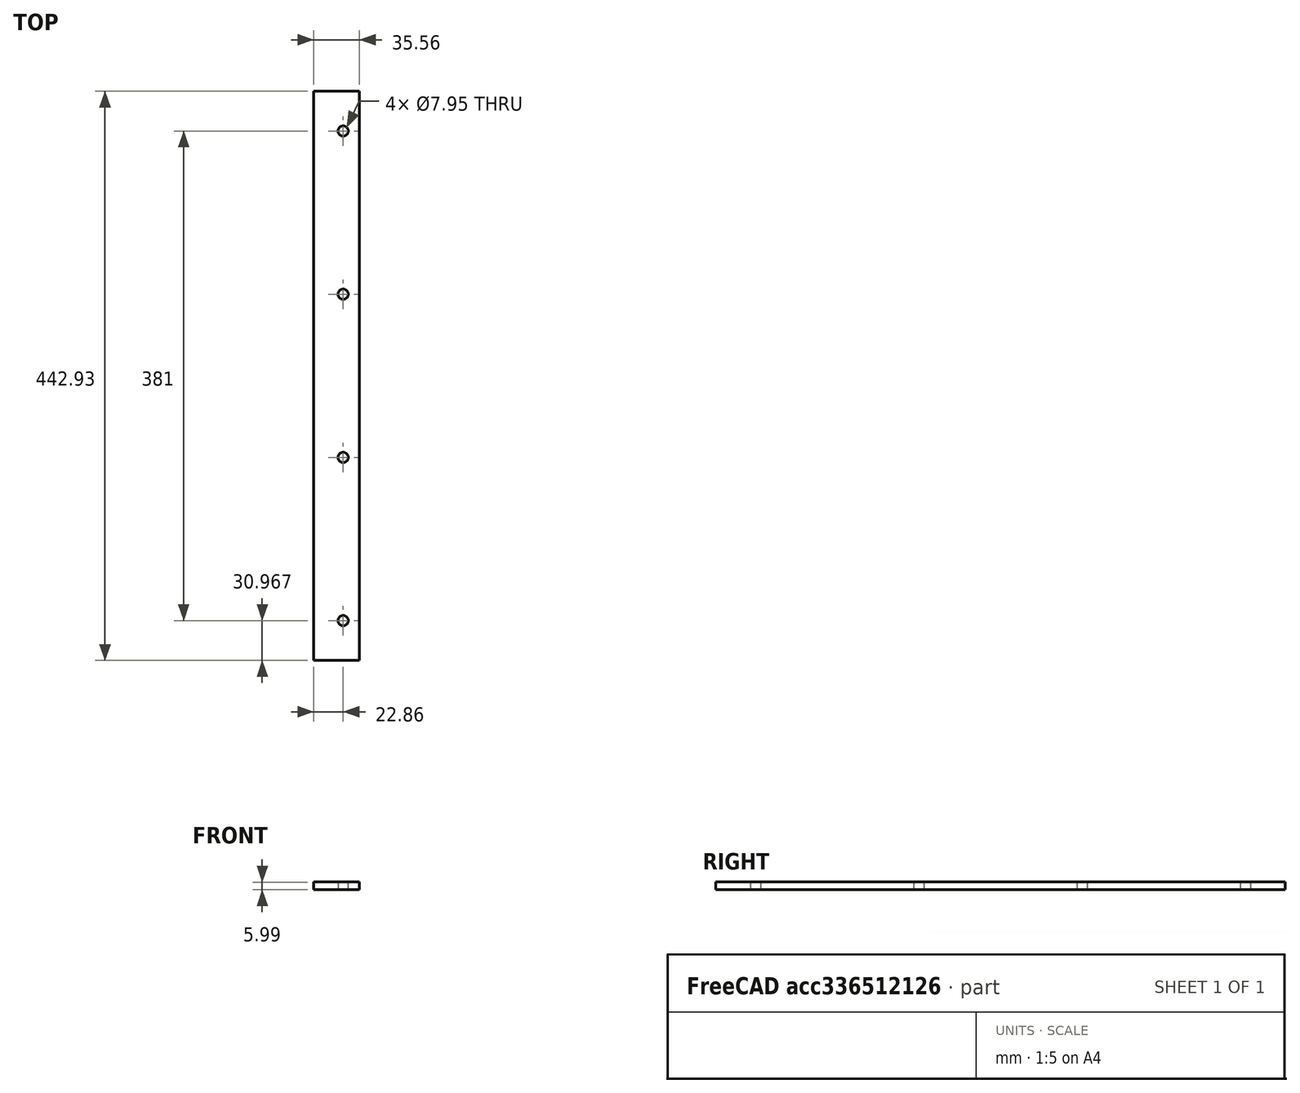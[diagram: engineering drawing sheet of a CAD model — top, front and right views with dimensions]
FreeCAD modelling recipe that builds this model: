
FCSTD DOCUMENT  (FreeCAD 0.19R24267 (Git))
Label: Up1-P10
License: All rights reserved
LicenseURL: http://en.wikipedia.org/wiki/All_rights_reserved
objects: TechDraw::DrawViewDimension×11, TechDraw::DrawProjGroupItem×2, TechDraw::DrawHatch×2, TechDraw::DrawViewAnnotation×2, Sketcher::SketchObject×1, Part::Extrusion×1, TechDraw::DrawSVGTemplate×1, TechDraw::DrawProjGroup×1, TechDraw::DrawPage×1
note: 2 computed .brp shape members not serialized (recipe doc carries the construction recipe); baked Part::Feature solids carry a one-line shape summary decoded from their .brp

FEATURE [Sketcher::SketchObject] Sketch
  FullyConstrained = true
  sketch-geometry (9):
    g0: LineSegment StartX=0 StartY=0 StartZ=0 EndX=35.56 EndY=0 EndZ=0
    g1: LineSegment StartX=35.56 StartY=0 StartZ=0 EndX=35.56 EndY=-442.925 EndZ=0
    g2: LineSegment StartX=35.56 StartY=-442.925 StartZ=0 EndX=0 EndY=-442.925 EndZ=0
    g3: LineSegment StartX=0 StartY=-442.925 StartZ=0 EndX=0 EndY=0 EndZ=0
    g4: Circle CenterX=22.86 CenterY=-30.9626 CenterZ=0 NormalX=0 NormalY=0 NormalZ=1 AngleXU=0 Radius=3.9751
    g5: Circle CenterX=22.86 CenterY=-157.963 CenterZ=0 NormalX=0 NormalY=0 NormalZ=1 AngleXU=0 Radius=3.9751
    g6: Circle CenterX=22.86 CenterY=-284.963 CenterZ=0 NormalX=0 NormalY=0 NormalZ=1 AngleXU=0 Radius=3.9751
    g7: Circle CenterX=22.86 CenterY=-411.963 CenterZ=0 NormalX=0 NormalY=0 NormalZ=1 AngleXU=0 Radius=3.9751
    g8: LineSegment StartX=22.86 StartY=0 StartZ=0 EndX=22.86 EndY=-442.925 EndZ=0
  constraints (27):
    c: Coincident(g0,g1)
    c: Coincident(g1,g2)
    c: Coincident(g2,g3)
    c: Coincident(g3,g0)
    c: Horizontal(g0)
    c: Horizontal(g2)
    c: Vertical(g1)
    c: Vertical(g3)
    c: Coincident(g0,g-1)
    c: DistanceY(g3,g3) = 442.925
    c: DistanceX(g0,g0) = 35.56
    c: Diameter(g4) = 7.9502
    c: Equal(g5,g6)
    c: Equal(g6,g7)
    c: Equal(g7,g4)
    c: PointOnObject(g8,g0)
    c: PointOnObject(g8,g2)
    c: Vertical(g8)
    c: Distance(g8,g1) = 12.7
    c: PointOnObject(g4,g8)
    c: PointOnObject(g5,g8)
    c: PointOnObject(g6,g8)
    c: PointOnObject(g7,g8)
    c: Distance(g4,g0) = 30.9626
    c: Distance(g5,g0) = 157.963
    c: Distance(g6,g0) = 284.963
    c: Distance(g7,g0) = 411.963
FEATURE [Part::Extrusion] Extrude
  Base = -> Sketch
  Dir = (0,0,1)
  DirMode = 2
  FaceMakerClass = Part::FaceMakerBullseye
  LengthFwd = 5.9944
  LengthRev = 0
  Solid = true
  Symmetric = false
FEATURE [TechDraw::DrawSVGTemplate] Template
  Height = 215.9
  Orientation = 1
  Width = 279.4
FEATURE [TechDraw::DrawProjGroupItem] ProjItem  label="Front"
  CoarseView = false
  Direction = (0,0,1)
  Focus = 100
  HardHidden = false
  IsoCount = 0
  IsoHidden = false
  IsoVisible = false
  LockPosition = true
  Perspective = false
  Rotation = 0
  RotationVector = (1,0,0)
  Scale = 0.25
  ScaleType = 2
  SeamHidden = false
  SeamVisible = true
  SmoothHidden = false
  SmoothVisible = true
  Source = -> [Extrude]
  Type = 0
  X = 0
  XDirection = (1,0,0)
  Y = 0
FEATURE [TechDraw::DrawProjGroupItem] ProjItem001  label="Left"
  CoarseView = false
  Direction = (-1,0,1e-16)
  Focus = 100
  HardHidden = false
  IsoCount = 0
  IsoHidden = false
  IsoVisible = false
  LockPosition = false
  Perspective = false
  Rotation = 0
  RotationVector = (1,0,0)
  ScaleType = 2
  SeamHidden = false
  SeamVisible = true
  SmoothHidden = false
  SmoothVisible = true
  Source = -> [Extrude]
  Type = 1
  X = 67.7026
  XDirection = (1e-16,0,1)
  Y = 0
FEATURE [TechDraw::DrawProjGroup] ProjGroup
  Anchor = -> ProjItem
  AutoDistribute = true
  LockPosition = false
  ProjectionType = 0
  Rotation = 0
  Scale = 0.25
  ScaleType = 2
  Source = -> [Extrude]
  Views = -> [ProjItem,ProjItem001]
  X = 139.7
  Y = 107.95
  spacingX = 15.0114
  spacingY = 15.0114
FEATURE [TechDraw::DrawHatch] Hatch  label="HatchF0"
  HatchPattern = <path>
  Source = -> ProjItem [Face0]
FEATURE [TechDraw::DrawHatch] Hatch001  label="Hatch001F0"
  HatchPattern = <path>
  Source = -> ProjItem001 [Face0]
FEATURE [TechDraw::DrawViewDimension] Dimension
  Arbitrary = false
  ArbitraryTolerances = false
  EqualTolerance = true
  FormatSpec = %.3f
  FormatSpecOverTolerance = %+.3f
  FormatSpecUnderTolerance = %+.3f
  Inverted = false
  LockPosition = false
  MeasureType = 1
  OverTolerance = 0
  References2D = -> [ProjItem]
  Rotation = 0
  ScaleType = 0
  TheoreticalExact = false
  Type = 1
  UnderTolerance = 0
  X = -26.4635
  Y = 73.6993
FEATURE [TechDraw::DrawViewDimension] Dimension001
  Arbitrary = false
  ArbitraryTolerances = false
  EqualTolerance = true
  FormatSpec = %.3f
  FormatSpecOverTolerance = %+.3f
  FormatSpecUnderTolerance = %+.3f
  Inverted = false
  LockPosition = false
  MeasureType = 1
  OverTolerance = 0
  References2D = -> [ProjItem001]
  Rotation = 0
  ScaleType = 0
  TheoreticalExact = false
  Type = 1
  UnderTolerance = 0
  X = 20.2009
  Y = 43.2944
FEATURE [TechDraw::DrawViewDimension] Dimension002
  Arbitrary = false
  ArbitraryTolerances = false
  EqualTolerance = true
  FormatSpec = %.3f
  FormatSpecOverTolerance = %+.3f
  FormatSpecUnderTolerance = %+.3f
  Inverted = false
  LockPosition = false
  MeasureType = 1
  OverTolerance = 0
  References2D = -> [ProjItem]
  Rotation = 0
  ScaleType = 0
  TheoreticalExact = false
  Type = 2
  UnderTolerance = 0
  X = 37.1003
  Y = 4.88984
FEATURE [TechDraw::DrawViewDimension] Dimension003
  Arbitrary = false
  ArbitraryTolerances = false
  EqualTolerance = true
  FormatSpec = %.3f
  FormatSpecOverTolerance = %+.3f
  FormatSpecUnderTolerance = %+.3f
  Inverted = false
  LockPosition = false
  MeasureType = 1
  OverTolerance = 0
  References2D = -> [ProjItem]
  Rotation = 0
  ScaleType = 0
  TheoreticalExact = false
  Type = 2
  UnderTolerance = 0
  X = -15.6802
  Y = 38.5606
FEATURE [TechDraw::DrawViewDimension] Dimension004
  Arbitrary = false
  ArbitraryTolerances = false
  EqualTolerance = true
  FormatSpec = %.3f
  FormatSpecOverTolerance = %+.3f
  FormatSpecUnderTolerance = %+.3f
  Inverted = false
  LockPosition = false
  MeasureType = 1
  OverTolerance = 0
  References2D = -> [ProjItem]
  Rotation = 0
  ScaleType = 0
  TheoreticalExact = false
  Type = 2
  UnderTolerance = 0
  X = -23.4227
  Y = 36.4299
FEATURE [TechDraw::DrawViewDimension] Dimension005
  Arbitrary = false
  ArbitraryTolerances = false
  EqualTolerance = true
  FormatSpec = %.3f
  FormatSpecOverTolerance = %+.3f
  FormatSpecUnderTolerance = %+.3f
  Inverted = false
  LockPosition = false
  MeasureType = 1
  OverTolerance = 0
  References2D = -> [ProjItem]
  Rotation = 0
  ScaleType = 0
  TheoreticalExact = false
  Type = 2
  UnderTolerance = 0
  X = -31.083
  Y = 21.0224
FEATURE [TechDraw::DrawViewDimension] Dimension006
  Arbitrary = false
  ArbitraryTolerances = false
  EqualTolerance = true
  FormatSpec = %.3f
  FormatSpecOverTolerance = %+.3f
  FormatSpecUnderTolerance = %+.3f
  Inverted = false
  LockPosition = false
  MeasureType = 1
  OverTolerance = 0
  References2D = -> [ProjItem]
  Rotation = 0
  ScaleType = 0
  TheoreticalExact = false
  Type = 2
  UnderTolerance = 0
  X = -38.8342
  Y = 5.26931
FEATURE [TechDraw::DrawViewDimension] Dimension007
  Arbitrary = false
  ArbitraryTolerances = false
  EqualTolerance = true
  FormatSpec = ⌀%.3f
  FormatSpecOverTolerance = %+.3f
  FormatSpecUnderTolerance = %+.3f
  Inverted = false
  LockPosition = false
  MeasureType = 1
  OverTolerance = 0
  References2D = -> [ProjItem]
  Rotation = 0
  ScaleType = 0
  TheoreticalExact = false
  Type = 5
  UnderTolerance = 0
  X = 21.1512
  Y = 43.5768
FEATURE [TechDraw::DrawViewDimension] Dimension008
  Arbitrary = false
  ArbitraryTolerances = false
  EqualTolerance = true
  FormatSpec = ⌀%.3f
  FormatSpecOverTolerance = %+.3f
  FormatSpecUnderTolerance = %+.3f
  Inverted = false
  LockPosition = false
  MeasureType = 1
  OverTolerance = 0
  References2D = -> [ProjItem]
  Rotation = 0
  ScaleType = 0
  TheoreticalExact = false
  Type = 5
  UnderTolerance = 0
  X = 17.6492
  Y = 15.3823
FEATURE [TechDraw::DrawViewDimension] Dimension009
  Arbitrary = false
  ArbitraryTolerances = false
  EqualTolerance = true
  FormatSpec = ⌀%.3f
  FormatSpecOverTolerance = %+.3f
  FormatSpecUnderTolerance = %+.3f
  Inverted = false
  LockPosition = false
  MeasureType = 1
  OverTolerance = 0
  References2D = -> [ProjItem]
  Rotation = 0
  ScaleType = 0
  TheoreticalExact = false
  Type = 5
  UnderTolerance = 0
  X = 17.2541
  Y = -16.0883
FEATURE [TechDraw::DrawViewDimension] Dimension010
  Arbitrary = false
  ArbitraryTolerances = false
  EqualTolerance = true
  FormatSpec = ⌀%.3f
  FormatSpecOverTolerance = %+.3f
  FormatSpecUnderTolerance = %+.3f
  Inverted = false
  LockPosition = false
  MeasureType = 1
  OverTolerance = 0
  References2D = -> [ProjItem]
  Rotation = 0
  ScaleType = 0
  TheoreticalExact = false
  Type = 5
  UnderTolerance = 0
  X = 16.3215
  Y = -46.1665
FEATURE [TechDraw::DrawViewAnnotation] Annotation
  Font = osifont
  LineSpace = 80
  LockPosition = false
  MaxWidth = -1
  Rotation = 0
  ScaleType = 0
  Text = Figure S3 (Upright) | Panel 10 [slide seal] | Quantity: 1
  TextSize = 5
  TextStyle = 0
  X = 30.8399
  Y = 195.58
FEATURE [TechDraw::DrawViewAnnotation] Annotation002
  Font = osifont
  LineSpace = 80
  LockPosition = false
  MaxWidth = -1
  Rotation = 0
  ScaleType = 0
  Text = Units: Inches
  TextSize = 5
  TextStyle = 0
  X = 259.08
  Y = 5.08
FEATURE [TechDraw::DrawPage] Page
  KeepUpdated = true
  NextBalloonIndex = 1
  ProjectionType = 0
  Template = -> Template
  Views = -> [ProjGroup,Dimension,Dimension001,Dimension002,Dimension003,Dimension004,Dimension005,Dimension006,Dimension007,Dimension008,Dimension009,Dimension010,Annotation,Annotation002]
note: 2 file-system paths scrubbed to <path> (originals preserved in the JSON sidecar)
